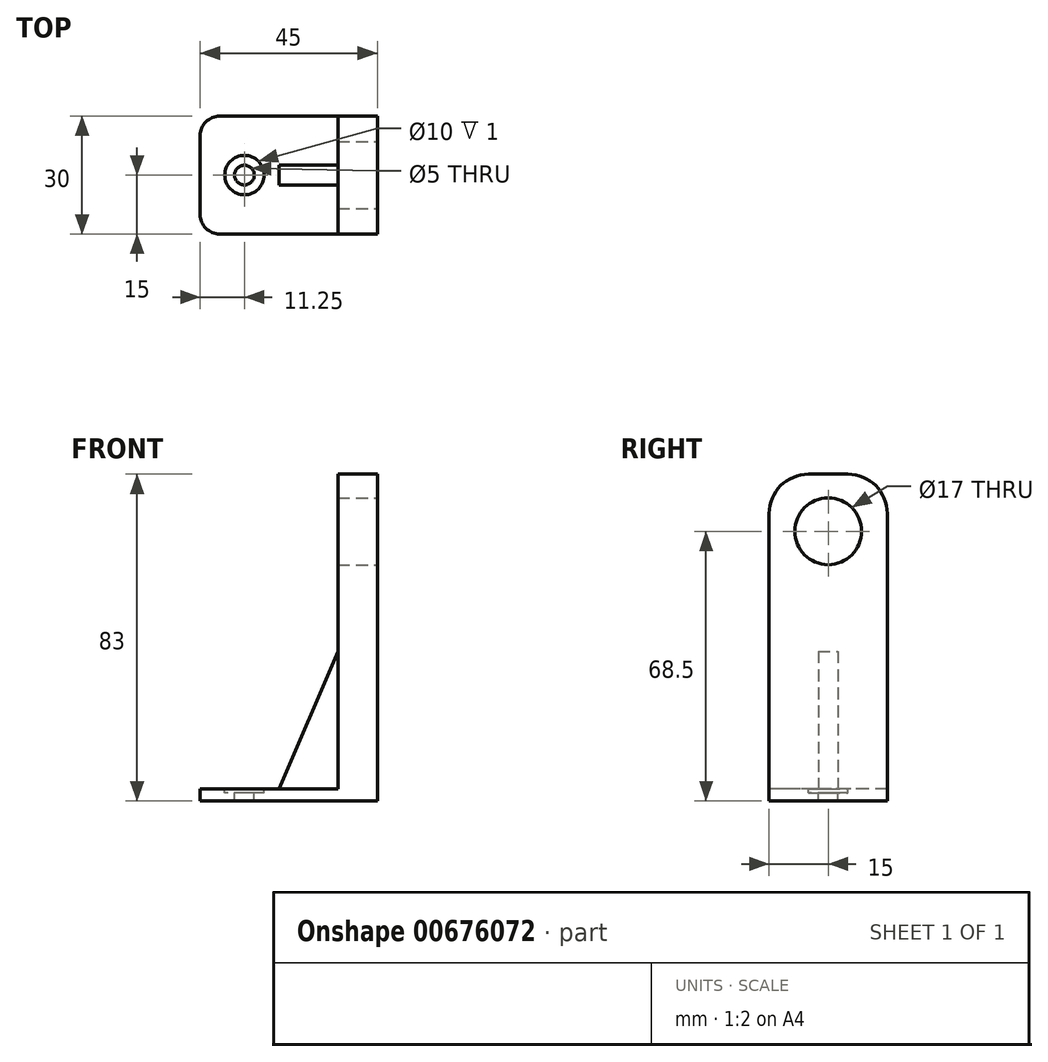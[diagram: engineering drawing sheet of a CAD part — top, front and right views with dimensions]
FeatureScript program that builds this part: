
annotation { "Feature Type Name" : "Feature", "Feature Type Description" : "" }
export const myFeature = defineFeature(function(context is Context, id is Id, definition is map)
    precondition{}
    {
        {
            var Q0;
            Q0=qCreatedBy(makeId("Top.planeOp"),FACE);
            var sketch = newSketch(context, id + "F0", { "sketchPlane" : qUnion([Q0])});
            skLineSegment(sketch, "E0.bottom", {"start": v(-22.5, 15) * mm, "end": v(22.5, 15) * mm});
            skLineSegment(sketch, "E0.top", {"start": v(-22.5, -15) * mm, "end": v(22.5, -15) * mm});
            skLineSegment(sketch, "E0.left", {"start": v(-22.5, 15) * mm, "end": v(-22.5, -15) * mm});
            skLineSegment(sketch, "E0.right", {"start": v(22.5, 15) * mm, "end": v(22.5, -15) * mm});
            skSolve(sketch);
        }
        {
            var Q0;
            Q0 = qSketchRegion(id + "F0", true);
            extrude(context, id + "F1", {"entities" : qUnion([Q0]), "depth" : 3 * mm, "offsetDistance" : 25 * mm});
        }
        {
            var Q0;
            Q0=makeQuery(id+"F1.opExtrude","CAP_FACE",FACE,{"disambiguationData":[OSD([sQuery(id+"F0.wireOp",EDGE,"E0.bottom"),sQuery(id+"F0.wireOp",EDGE,"E0.top"),sQuery(id+"F0.wireOp",EDGE,"E0.left"),sQuery(id+"F0.wireOp",EDGE,"E0.right")])],"isStart":false});
            var sketch = newSketch(context, id + "F2", { "sketchPlane" : qUnion([Q0])});
            skLineSegment(sketch, "E1", {"start": v(-22.5, 0) * mm, "end": v(0, 0) * mm, "construction": true});
            skCircle(sketch, "E2", {"center": v(-11.25, 0) * mm, "radius": 5 * mm});
            skSolve(sketch);
        }
        {
            var Q0;
            Q0 = qSketchRegion(id + "F2", true);
            extrude(context, id + "F3", {"entities" : qUnion([Q0]), "operationType" : NewBodyOperationType.REMOVE, "oppositeDirection" : true, "depth" : 1 * mm, "offsetDistance" : 25 * mm});
        }
        {
            var Q0;
            Q0=makeQuery(id+"F3.boolean.opBoolean","COPY",FACE,{"derivedFrom":makeQuery(id+"F3.opExtrude","CAP_FACE",FACE,{"disambiguationData":[OSD([sQuery(id+"F2.wireOp",EDGE,"E2")])],"isStart":false})});
            var sketch = newSketch(context, id + "F4", { "sketchPlane" : qUnion([Q0])});
            skCircle(sketch, "E3", {"center": v(-11.25, 0) * mm, "radius": 2.5 * mm});
            skSolve(sketch);
        }
        {
            var Q0;
            Q0 = qSketchRegion(id + "F4", true);
            extrude(context, id + "F5", {"entities" : qUnion([Q0]), "operationType" : NewBodyOperationType.REMOVE, "endBound" : BoundingType.UP_TO_NEXT, "oppositeDirection" : true, "depth" : 25 * mm, "offsetDistance" : 25 * mm});
        }
        {
            var Q0;
            Q0=makeQuery(id+"F1.opExtrude","CAP_FACE",FACE,{"disambiguationData":[OSD([sQuery(id+"F0.wireOp",EDGE,"E0.bottom"),sQuery(id+"F0.wireOp",EDGE,"E0.top"),sQuery(id+"F0.wireOp",EDGE,"E0.left"),sQuery(id+"F0.wireOp",EDGE,"E0.right")])],"isStart":false});
            var sketch = newSketch(context, id + "F6", { "sketchPlane" : qUnion([Q0])});
            skLineSegment(sketch, "E4.bottom", {"start": v(22.5, 15) * mm, "end": v(12.5, 15) * mm});
            skLineSegment(sketch, "E4.top", {"start": v(22.5, -15) * mm, "end": v(12.5, -15) * mm});
            skLineSegment(sketch, "E4.left", {"start": v(22.5, 15) * mm, "end": v(22.5, -15) * mm});
            skLineSegment(sketch, "E4.right", {"start": v(12.5, 15) * mm, "end": v(12.5, -15) * mm});
            skSolve(sketch);
        }
        {
            var Q0;
            Q0 = qSketchRegion(id + "F6", true);
            extrude(context, id + "F7", {"entities" : qUnion([Q0]), "operationType" : NewBodyOperationType.ADD, "depth" : 80 * mm, "offsetDistance" : 25 * mm});
        }
        {
            var Q0;
            Q0=qCreatedBy(makeId("Front.planeOp"),FACE);
            var sketch = newSketch(context, id + "F8", { "sketchPlane" : qUnion([Q0])});
            skPoint(sketch, "E5", {"position": v(12.5, 38) * mm});
            skPoint(sketch, "E6", {"position": v(-2.5, 3) * mm});
            skPoint(sketch, "E7", {"position": v(12.5, 3) * mm});
            skLineSegment(sketch, "E8", {"start": v(-2.5, 3) * mm, "end": v(12.5, 3) * mm});
            skLineSegment(sketch, "E9", {"start": v(12.5, 38) * mm, "end": v(12.5, 3) * mm});
            skLineSegment(sketch, "E10", {"start": v(-2.5, 3) * mm, "end": v(12.5, 38) * mm});
            skSolve(sketch);
        }
        {
            var Q0;
            Q0 = qSketchRegion(id + "F8", true);
            extrude(context, id + "F9", {"entities" : qUnion([Q0]), "operationType" : NewBodyOperationType.ADD, "endBound" : BoundingType.SYMMETRIC, "depth" : 5 * mm, "offsetDistance" : 25 * mm});
        }
        {
            var Q0;
            Q0=makeQuery(id+"F7.boolean.opBoolean","MERGE",FACE,{"derivedFrom":[makeQuery(id+"F1.opExtrude","SWEPT_FACE",FACE,{"disambiguationData":[OSD([sQuery(id+"F0.wireOp",EDGE,"E0.right")])]}),makeQuery(id+"F7.opExtrude","SWEPT_FACE",FACE,{"disambiguationData":[OSD([sQuery(id+"F6.wireOp",EDGE,"E4.left")])]})]});
            var sketch = newSketch(context, id + "F10", { "sketchPlane" : qUnion([Q0])});
            skCircle(sketch, "E11", {"center": v(0, 68.5) * mm, "radius": 8.5 * mm});
            skPoint(sketch, "E12", {"position": v(0, 77) * mm});
            skSolve(sketch);
        }
        {
            var Q0;
            Q0 = qSketchRegion(id + "F10", true);
            extrude(context, id + "F11", {"entities" : qUnion([Q0]), "operationType" : NewBodyOperationType.REMOVE, "endBound" : BoundingType.UP_TO_NEXT, "oppositeDirection" : true, "depth" : 25 * mm, "offsetDistance" : 25 * mm});
        }
        {
            var Q0;
            Q0=makeQuery(id+"F7.opExtrude","CAP_EDGE",EDGE,{"disambiguationData":[OSD([sQuery(id+"F6.wireOp",EDGE,"E4.bottom")])],"isStart":false});
            fillet(context, id + "F12", {"entities" : qUnion([Q0]), "radius" : 10 * mm, "tangentPropagation" : true, "allowEdgeOverflow" : false});
        }
        {
            var Q0;
            Q0=makeQuery(id+"F7.opExtrude","CAP_EDGE",EDGE,{"disambiguationData":[OSD([sQuery(id+"F6.wireOp",EDGE,"E4.top")])],"isStart":false});
            fillet(context, id + "F13", {"entities" : qUnion([Q0]), "radius" : 10 * mm, "tangentPropagation" : true, "allowEdgeOverflow" : false});
        }
        {
            var Q0;
            Q0=makeQuery(id+"F1.opExtrude","SWEPT_EDGE",EDGE,{"disambiguationData":[OSD([sQuery(id+"F0.wireOp",EDGE,"E0.bottom"),sQuery(id+"F0.wireOp",EDGE,"E0.left")])]});
            fillet(context, id + "F14", {"entities" : qUnion([Q0]), "radius" : 5 * mm, "tangentPropagation" : true, "allowEdgeOverflow" : false});
        }
        {
            var Q0;
            Q0=makeQuery(id+"F1.opExtrude","SWEPT_EDGE",EDGE,{"disambiguationData":[OSD([sQuery(id+"F0.wireOp",EDGE,"E0.top"),sQuery(id+"F0.wireOp",EDGE,"E0.left")])]});
            fillet(context, id + "F15", {"entities" : qUnion([Q0]), "radius" : 5 * mm, "tangentPropagation" : true, "allowEdgeOverflow" : false});
        }
    });
